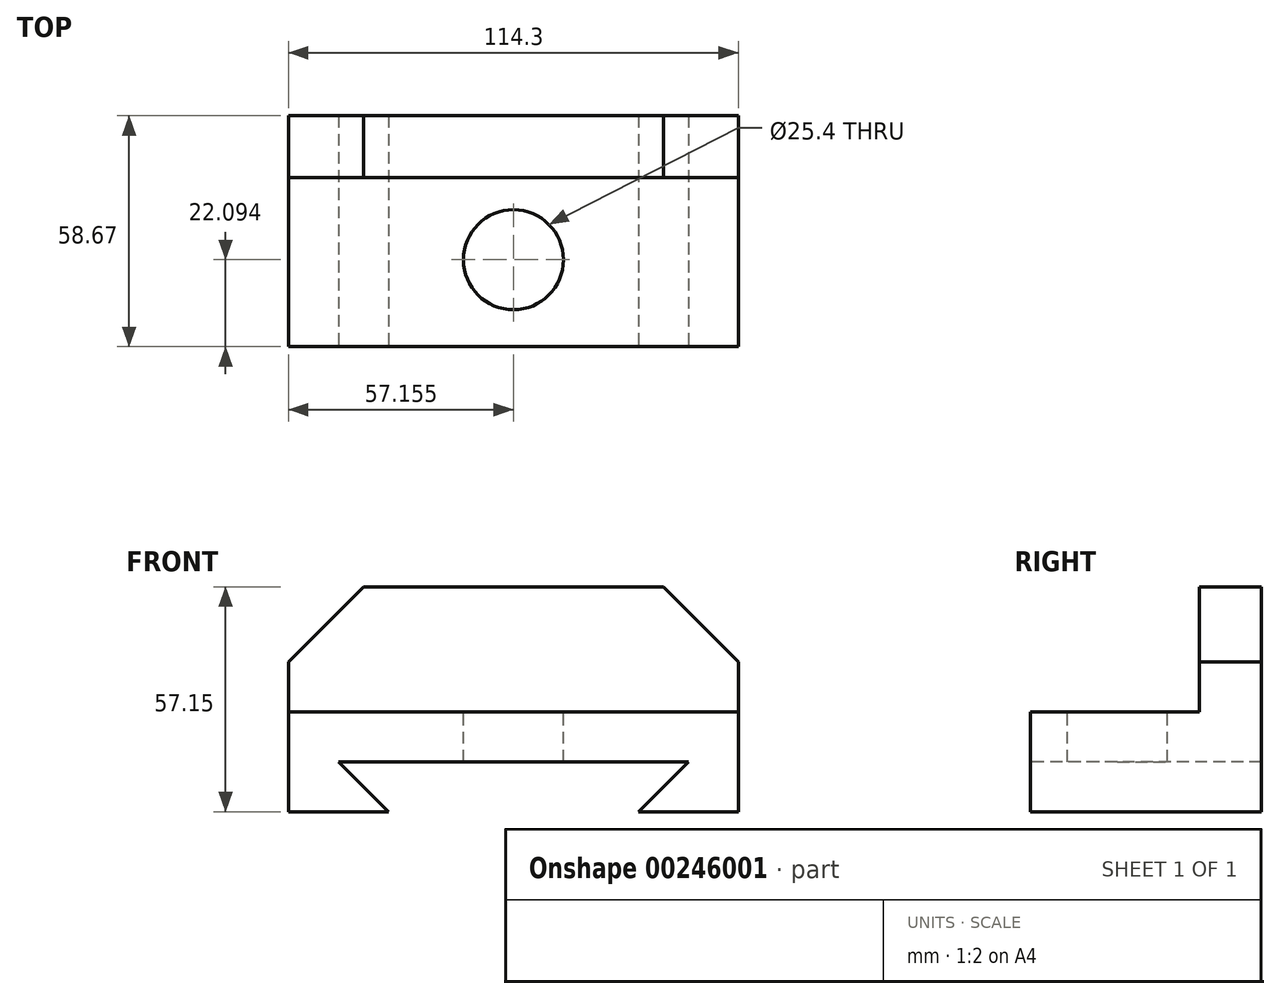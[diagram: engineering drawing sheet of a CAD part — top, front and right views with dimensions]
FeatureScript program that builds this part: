
annotation { "Feature Type Name" : "Feature", "Feature Type Description" : "" }
export const myFeature = defineFeature(function(context is Context, id is Id, definition is map)
    precondition{}
    {
        {
            var Q0;
            Q0=qCreatedBy(makeId("Front.planeOp"),FACE);
            var sketch = newSketch(context, id + "F0", { "sketchPlane" : qUnion([Q0])});
            skLineSegment(sketch, "E0", {"start": v(-86.96, -37.29) * mm, "end": v(27.34, -37.29) * mm});
            skLineSegment(sketch, "E1", {"start": v(27.34, -37.29) * mm, "end": v(27.34, 19.86) * mm});
            skLineSegment(sketch, "E2", {"start": v(27.34, 19.86) * mm, "end": v(-86.96, 19.86) * mm});
            skLineSegment(sketch, "E3", {"start": v(-86.96, 19.86) * mm, "end": v(-86.96, -37.29) * mm});
            skSolve(sketch);
        }
        {
            var Q0;
            Q0 = qSketchRegion(id + "F0", true);
            extrude(context, id + "F1", {"entities" : qUnion([Q0]), "depth" : 58.67 * mm});
        }
        {
            var Q0;
            Q0=makeQuery(id+"F1.opExtrude","SWEPT_FACE",FACE,{"disambiguationData":[OSD([sQuery(id+"F0.wireOp",EDGE,"E2")])]});
            var sketch = newSketch(context, id + "F2", { "sketchPlane" : qUnion([Q0])});
            skLineSegment(sketch, "E4", {"start": v(-86.96, -58.67) * mm, "end": v(-86.96, -15.75) * mm});
            skLineSegment(sketch, "E5", {"start": v(-86.96, -15.75) * mm, "end": v(27.34, -15.75) * mm});
            skLineSegment(sketch, "E6", {"start": v(27.34, -15.75) * mm, "end": v(27.34, -58.67) * mm});
            skLineSegment(sketch, "E7", {"start": v(27.34, -58.67) * mm, "end": v(-86.96, -58.67) * mm});
            skSolve(sketch);
        }
        {
            var Q0;
            Q0 = qSketchRegion(id + "F2", true);
            extrude(context, id + "F3", {"entities" : qUnion([Q0]), "operationType" : NewBodyOperationType.REMOVE, "oppositeDirection" : true, "depth" : 31.75 * mm});
        }
        {
            var Q0;
            Q0=makeQuery(id+"F3.boolean.opBoolean","COPY",FACE,{"derivedFrom":makeQuery(id+"F3.opExtrude","SWEPT_FACE",FACE,{"disambiguationData":[OSD([sQuery(id+"F2.wireOp",EDGE,"E5")])]})});
            var sketch = newSketch(context, id + "F4", { "sketchPlane" : qUnion([Q0])});
            skLineSegment(sketch, "E8", {"start": v(27.34, 19.86) * mm, "end": v(8.3, 19.86) * mm});
            skLineSegment(sketch, "E9", {"start": v(-86.96, 19.86) * mm, "end": v(-67.9, 19.86) * mm});
            skLineSegment(sketch, "E10", {"start": v(27.34, 19.86) * mm, "end": v(27.34, 0.81) * mm});
            skLineSegment(sketch, "E11", {"start": v(8.3, 19.86) * mm, "end": v(27.34, 0.81) * mm});
            skLineSegment(sketch, "E12", {"start": v(-86.96, 19.86) * mm, "end": v(-86.96, 0.81) * mm});
            skLineSegment(sketch, "E13", {"start": v(-67.9, 19.86) * mm, "end": v(-86.96, 0.81) * mm});
            skSolve(sketch);
        }
        {
            var Q0;
            Q0 = qSketchRegion(id + "F4", true);
            extrude(context, id + "F5", {"entities" : qUnion([Q0]), "operationType" : NewBodyOperationType.REMOVE, "oppositeDirection" : true, "depth" : 15.75 * mm});
        }
        {
            var Q0;
            Q0=makeQuery(id+"F1.opExtrude","CAP_FACE",FACE,{"disambiguationData":[OSD([sQuery(id+"F0.wireOp",EDGE,"E0"),sQuery(id+"F0.wireOp",EDGE,"E1"),sQuery(id+"F0.wireOp",EDGE,"E2"),sQuery(id+"F0.wireOp",EDGE,"E3")])],"isStart":false});
            var sketch = newSketch(context, id + "F6", { "sketchPlane" : qUnion([Q0])});
            skLineSegment(sketch, "E14", {"start": v(-29.8, -37.29) * mm, "end": v(1.94, -37.29) * mm});
            skLineSegment(sketch, "E15", {"start": v(-29.8, -37.29) * mm, "end": v(-61.56, -37.29) * mm});
            skPoint(sketch, "E16.endSnap0", {"position": v(27.34, -24.59) * mm});
            skLineSegment(sketch, "E17", {"start": v(-29.8, -37.29) * mm, "end": v(-29.8, -24.59) * mm});
            skLineSegment(sketch, "E18", {"start": v(-29.8, -24.59) * mm, "end": v(14.64, -24.59) * mm});
            skLineSegment(sketch, "E19", {"start": v(-29.8, -24.59) * mm, "end": v(-74.26, -24.59) * mm});
            skLineSegment(sketch, "E20", {"start": v(-74.26, -24.59) * mm, "end": v(-61.56, -37.29) * mm});
            skLineSegment(sketch, "E21", {"start": v(1.94, -37.29) * mm, "end": v(14.64, -24.59) * mm});
            skSolve(sketch);
        }
        {
            var Q0;
            Q0=makeQuery(id+"F3.boolean.opBoolean","COPY",FACE,{"derivedFrom":makeQuery(id+"F3.opExtrude","CAP_FACE",FACE,{"disambiguationData":[OSD([sQuery(id+"F2.wireOp",EDGE,"E4"),sQuery(id+"F2.wireOp",EDGE,"E5"),sQuery(id+"F2.wireOp",EDGE,"E6"),sQuery(id+"F2.wireOp",EDGE,"E7")])],"isStart":false})});
            var sketch = newSketch(context, id + "F7", { "sketchPlane" : qUnion([Q0])});
            skLineSegment(sketch, "E22", {"start": v(-86.96, -58.67) * mm, "end": v(-86.96, -36.58) * mm});
            skCircle(sketch, "E23", {"center": v(-29.8, -36.58) * mm, "radius": 12.7 * mm});
            skPoint(sketch, "E23.centerSnap0", {"position": v(-29.8, -58.67) * mm});
            skSolve(sketch);
        }
        {
            var Q0;
            Q0 = qSketchRegion(id + "F7", true);
            extrude(context, id + "F8", {"entities" : qUnion([Q0]), "operationType" : NewBodyOperationType.REMOVE, "oppositeDirection" : true, "depth" : 25.4 * mm});
        }
        {
            var Q0;
            Q0 = qSketchRegion(id + "F6", true);
            extrude(context, id + "F9", {"entities" : qUnion([Q0]), "operationType" : NewBodyOperationType.REMOVE, "oppositeDirection" : true, "depth" : 58.67 * mm});
        }
    });
